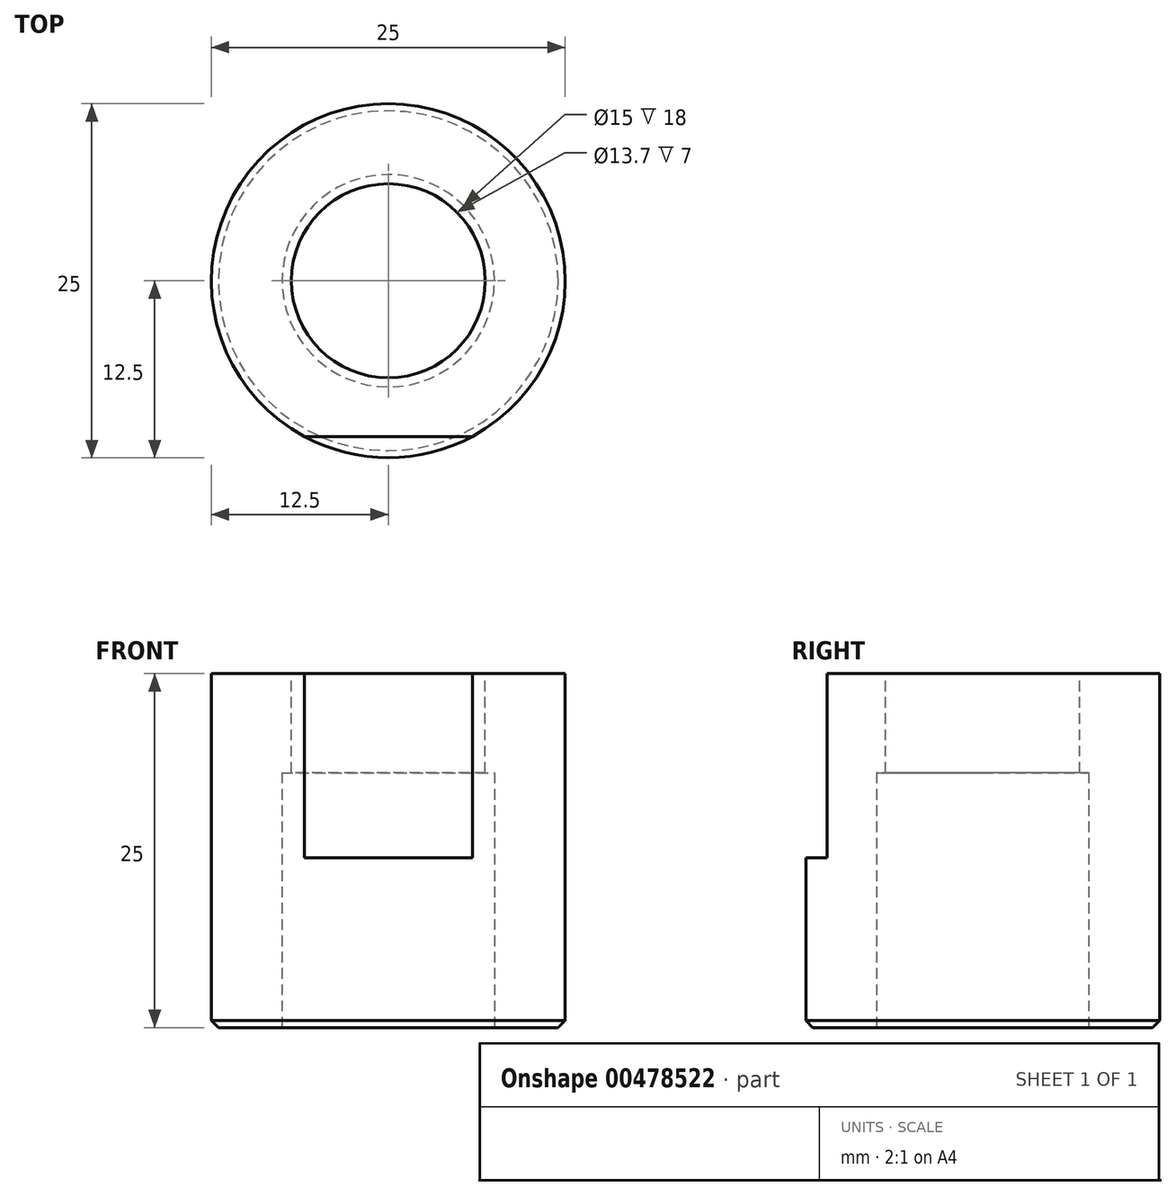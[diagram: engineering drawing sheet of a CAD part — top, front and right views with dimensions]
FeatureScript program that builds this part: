
annotation { "Feature Type Name" : "Feature", "Feature Type Description" : "" }
export const myFeature = defineFeature(function(context is Context, id is Id, definition is map)
    precondition{}
    {
        {
            var Q0;
            Q0=qCreatedBy(makeId("Top.planeOp"),FACE);
            var sketch = newSketch(context, id + "F0", { "sketchPlane" : qUnion([Q0])});
            skCircle(sketch, "E0", {"center": v(0, 0) * mm, "radius": 12.5 * mm});
            skSolve(sketch);
        }
        {
            var Q0;
            Q0 = qSketchRegion(id + "F0", true);
            extrude(context, id + "F1", {"entities" : qUnion([Q0]), "depth" : 25 * mm});
        }
        {
            var Q0;
            Q0=makeQuery(id+"F1.opExtrude","CAP_FACE",FACE,{"disambiguationData":[OSD([sQuery(id+"F0.wireOp",EDGE,"E0")])],"isStart":true});
            var sketch = newSketch(context, id + "F2", { "sketchPlane" : qUnion([Q0])});
            skCircle(sketch, "E1", {"center": v(0, 0) * mm, "radius": 7.5 * mm});
            skSolve(sketch);
        }
        {
            var Q0;
            Q0=makeQuery(id+"F2.imprint","IMPRINT",FACE,{"disambiguationData":[TD([[makeQuery(id+"F2.imprint","IMPRINT",EDGE,{"derivedFrom":sQuery(id+"F2.wireOp",EDGE,"E1")}),1.0]])]});
            extrude(context, id + "F3", {"entities" : qUnion([Q0]), "operationType" : NewBodyOperationType.REMOVE, "oppositeDirection" : true, "depth" : 18 * mm});
        }
        {
            var Q0;
            Q0=makeQuery(id+"F1.opExtrude","CAP_FACE",FACE,{"disambiguationData":[OSD([sQuery(id+"F0.wireOp",EDGE,"E0")])],"isStart":false});
            var sketch = newSketch(context, id + "F4", { "sketchPlane" : qUnion([Q0])});
            skCircle(sketch, "E2", {"center": v(0, 0) * mm, "radius": 6.85 * mm});
            skSolve(sketch);
        }
        {
            var Q0;
            Q0 = qSketchRegion(id + "F4", true);
            extrude(context, id + "F5", {"entities" : qUnion([Q0]), "operationType" : NewBodyOperationType.REMOVE, "oppositeDirection" : true, "depth" : 7 * mm});
        }
        {
            var Q0;
            Q0=makeQuery(id+"F1.opExtrude","CAP_FACE",FACE,{"disambiguationData":[OSD([sQuery(id+"F0.wireOp",EDGE,"E0")])],"isStart":false});
            var sketch = newSketch(context, id + "F6", { "sketchPlane" : qUnion([Q0])});
            skLineSegment(sketch, "E3", {"start": v(0, -12.5) * mm, "end": v(0, -11) * mm});
            skLineSegment(sketch, "E4", {"start": v(0, -11) * mm, "end": v(5.94, -11) * mm});
            skLineSegment(sketch, "E5", {"start": v(5.94, -11) * mm, "end": v(-5.94, -11) * mm});
            skArc(sketch, "E6", {"start": v(-5.94, -11) * mm, "mid": v(0, -12.5) * mm, "end": v(5.94, -11) * mm});
            skSolve(sketch);
        }
        {
            var Q0;
            Q0 = qSketchRegion(id + "F6", true);
            extrude(context, id + "F7", {"entities" : qUnion([Q0]), "operationType" : NewBodyOperationType.REMOVE, "oppositeDirection" : true, "depth" : 13 * mm});
        }
        {
            var Q0;
            Q0=makeQuery(id+"F1.opExtrude","CAP_EDGE",EDGE,{"disambiguationData":[OSD([sQuery(id+"F0.wireOp",EDGE,"E0")])],"isStart":true});
            chamfer(context, id + "F8", {"entities" : qUnion([Q0]), "width" : .5 * mm, "tangentPropagation" : true});
        }
    });
